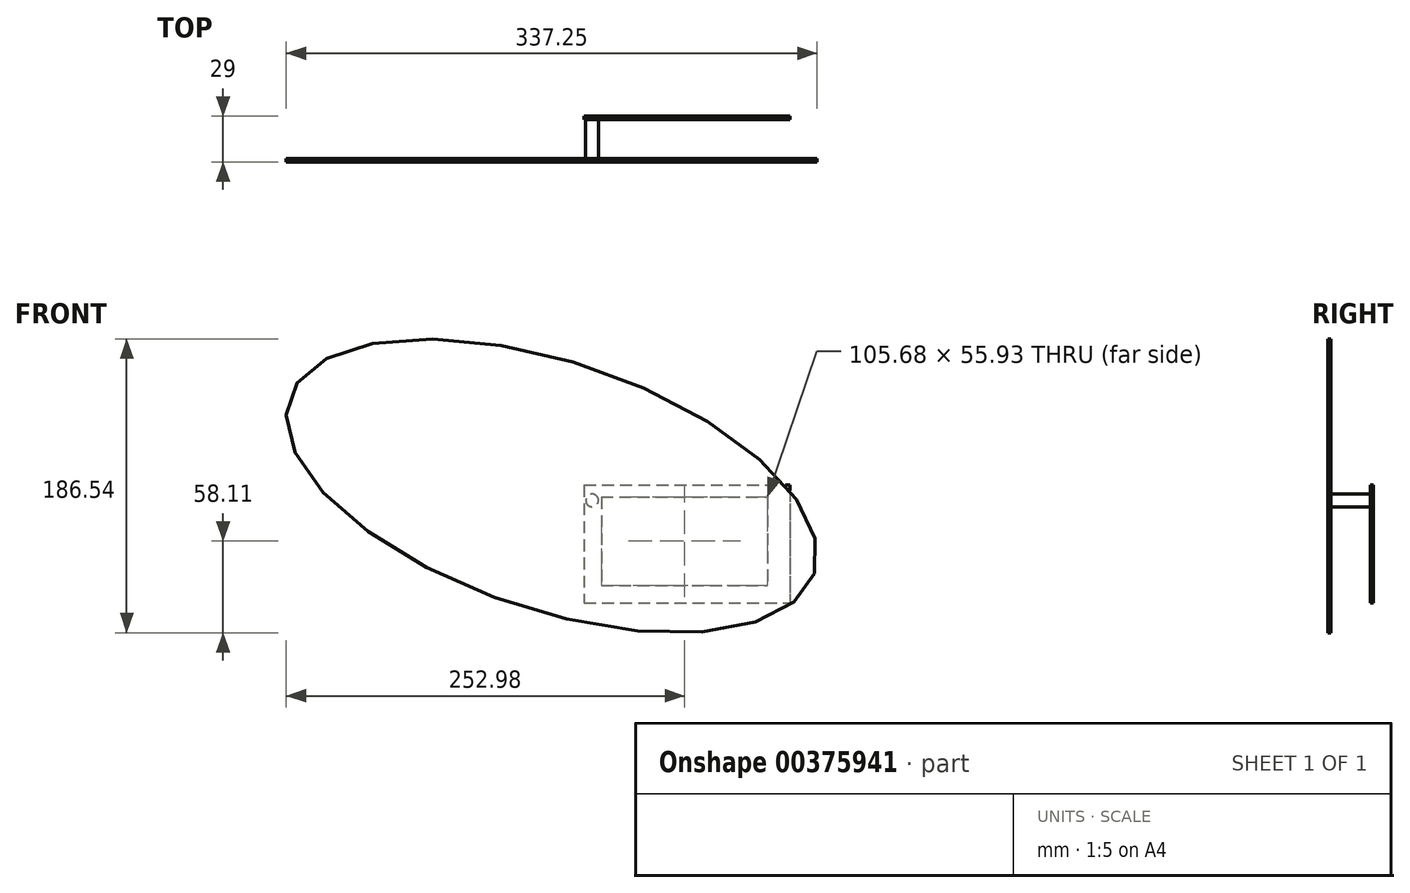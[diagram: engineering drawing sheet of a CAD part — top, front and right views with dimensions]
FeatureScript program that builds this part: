
annotation { "Feature Type Name" : "Feature", "Feature Type Description" : "" }
export const myFeature = defineFeature(function(context is Context, id is Id, definition is map)
    precondition{}
    {
        {
            var Q0;
            Q0=qCreatedBy(makeId("Front.planeOp"),FACE);
            var sketch = newSketch(context, id + "F0", { "sketchPlane" : qUnion([Q0])});
            skLineSegment(sketch, "E0.bottom", {"start": v(-63.8, 40.93) * mm, "end": v(66.83, 40.93) * mm});
            skLineSegment(sketch, "E0.top", {"start": v(-63.8, -34.01) * mm, "end": v(66.83, -34.01) * mm});
            skLineSegment(sketch, "E0.left", {"start": v(-63.8, 40.93) * mm, "end": v(-63.8, -34.01) * mm});
            skLineSegment(sketch, "E0.right", {"start": v(66.83, 40.93) * mm, "end": v(66.83, -34.01) * mm});
            skLineSegment(sketch, "E1.bottom", {"start": v(-52.84, 33.3) * mm, "end": v(52.84, 33.3) * mm});
            skLineSegment(sketch, "E1.top", {"start": v(-52.84, -22.63) * mm, "end": v(52.84, -22.63) * mm});
            skLineSegment(sketch, "E1.left", {"start": v(-52.84, 33.3) * mm, "end": v(-52.84, -22.63) * mm});
            skLineSegment(sketch, "E1.right", {"start": v(52.84, 33.3) * mm, "end": v(52.84, -22.63) * mm});
            skSolve(sketch);
        }
        {
            var Q0;
            Q0=qSketchRegion(id+"F0",true);
            extrude(context, id + "F1", {"entities" : qUnion([Q0]), "depth" : 2 * mm});
        }
        {
            var Q0;
            Q0=makeQuery(id+"F1.opExtrude","CAP_FACE",FACE,{"disambiguationData":[OSD([sQuery(id+"F0.wireOp",EDGE,"E0.bottom"),sQuery(id+"F0.wireOp",EDGE,"E0.top"),sQuery(id+"F0.wireOp",EDGE,"E0.left"),sQuery(id+"F0.wireOp",EDGE,"E0.right"),sQuery(id+"F0.wireOp",EDGE,"E1.bottom"),sQuery(id+"F0.wireOp",EDGE,"E1.top"),sQuery(id+"F0.wireOp",EDGE,"E1.left"),sQuery(id+"F0.wireOp",EDGE,"E1.right")])],"isStart":false});
            var sketch = newSketch(context, id + "F2", { "sketchPlane" : qUnion([Q0])});
            skCircle(sketch, "E2", {"center": v(-58.67, 31.24) * mm, "radius": 4.04 * mm});
            skSolve(sketch);
        }
        {
            var Q0;
            Q0=qSketchRegion(id+"F2",true);
            extrude(context, id + "F3", {"entities" : qUnion([Q0]), "operationType" : NewBodyOperationType.ADD, "depth" : 25 * mm});
        }
        {
            var Q0;
            Q0=makeQuery(id+"F3.opExtrude","CAP_FACE",FACE,{"disambiguationData":[OSD([sQuery(id+"F2.wireOp",EDGE,"E2")])],"isStart":false});
            var sketch = newSketch(context, id + "F4", { "sketchPlane" : qUnion([Q0])});
            skEllipse(sketch, "E3", {"center": v(-84.36, 40.5) * mm, "majorRadius": 175.8 * mm, "minorRadius": 78.94 * mm, "majorAxis": v(0.95, -0.32)});
            skSolve(sketch);
        }
        {
            var Q0;
            Q0=qSketchRegion(id+"F4",true);
            extrude(context, id + "F5", {"entities" : qUnion([Q0]), "depth" : 2 * mm});
        }
    });
